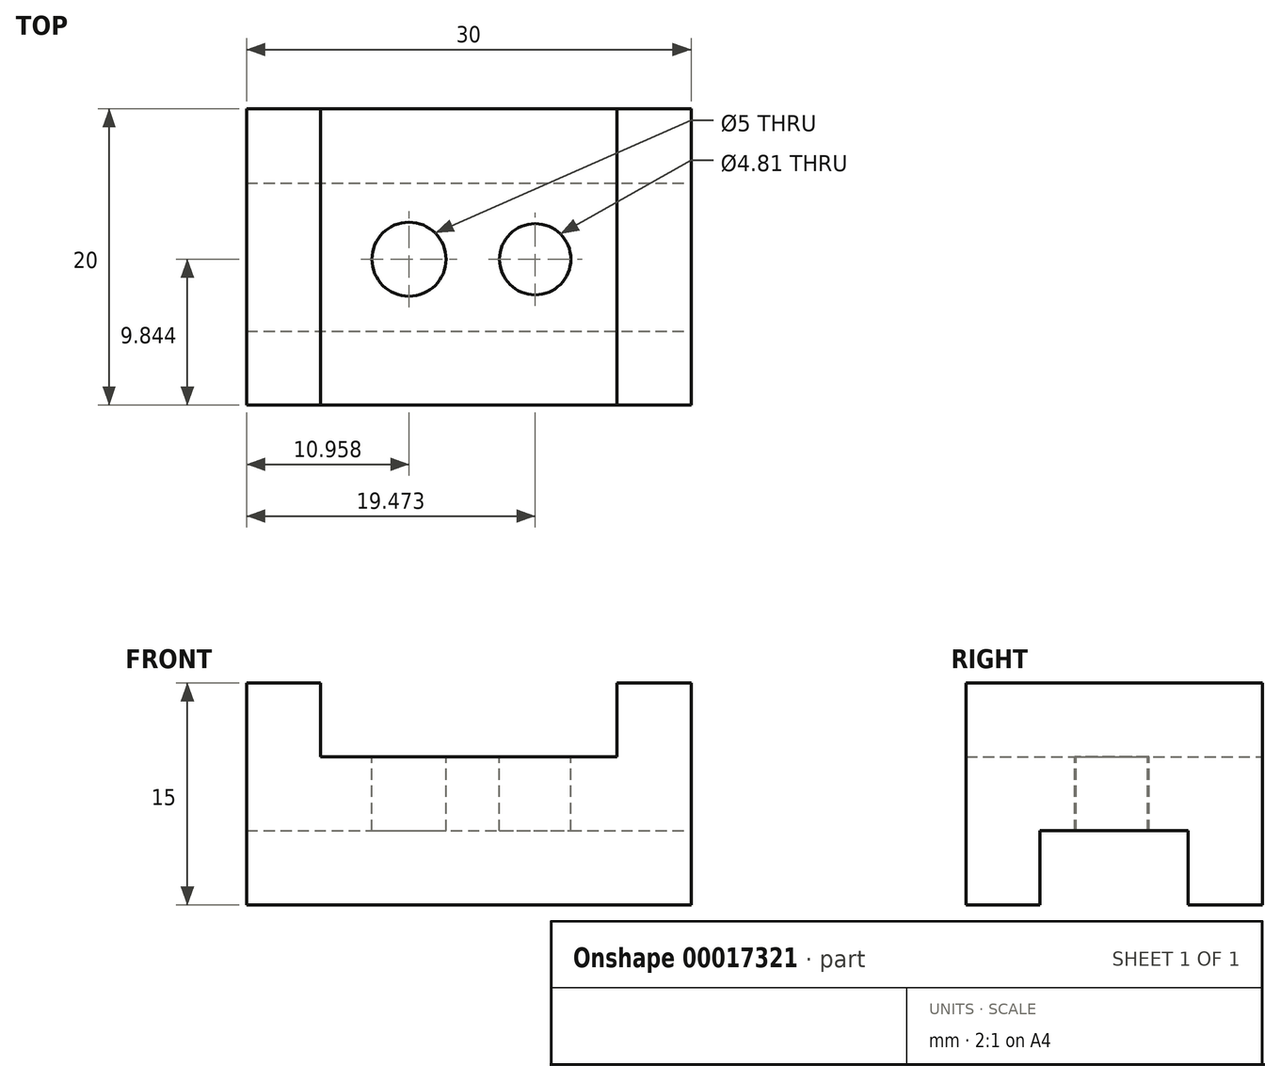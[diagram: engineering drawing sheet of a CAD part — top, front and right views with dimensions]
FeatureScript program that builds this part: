
annotation { "Feature Type Name" : "Feature", "Feature Type Description" : "" }
export const myFeature = defineFeature(function(context is Context, id is Id, definition is map)
    precondition{}
    {
        {
            var Q0;
            Q0=qCreatedBy(makeId("Front.planeOp"),FACE);
            var sketch = newSketch(context, id + "F0", { "sketchPlane" : qUnion([Q0])});
            skLineSegment(sketch, "E0", {"start": v(-34.67, 12.97) * mm, "end": v(-34.67, -2.03) * mm});
            skLineSegment(sketch, "E1", {"start": v(-34.67, 12.97) * mm, "end": v(-29.67, 12.97) * mm});
            skLineSegment(sketch, "E2", {"start": v(-29.67, 12.97) * mm, "end": v(-29.67, 7.97) * mm});
            skLineSegment(sketch, "E3", {"start": v(-29.67, 7.97) * mm, "end": v(-9.67, 7.97) * mm});
            skLineSegment(sketch, "E4", {"start": v(-9.67, 7.97) * mm, "end": v(-9.67, 12.97) * mm});
            skLineSegment(sketch, "E5", {"start": v(-4.67, 12.97) * mm, "end": v(-4.67, -2.03) * mm});
            skLineSegment(sketch, "E6", {"start": v(-4.67, -2.03) * mm, "end": v(-34.67, -2.03) * mm});
            skLineSegment(sketch, "E7", {"start": v(-4.67, 12.97) * mm, "end": v(-9.67, 12.97) * mm});
            skSolve(sketch);
        }
        {
            var Q0;
            Q0=makeQuery(id+"F0.imprint","IMPRINT",FACE,{"disambiguationData":[TD([[makeQuery(id+"F0.imprint","IMPRINT",EDGE,{"derivedFrom":sQuery(id+"F0.wireOp",EDGE,"E0")}),1.0]])]});
            extrude(context, id + "F1", {"entities" : qUnion([Q0]), "depth" : 20 * mm});
        }
        {
            var Q0;
            Q0=makeQuery(id+"F1.opExtrude","SWEPT_FACE",FACE,{"disambiguationData":[OSD([sQuery(id+"F0.wireOp",EDGE,"E3")])]});
            var sketch = newSketch(context, id + "F2", { "sketchPlane" : qUnion([Q0])});
            skCircle(sketch, "E8", {"center": v(-23.71, -10.16) * mm, "radius": 2.5 * mm});
            skCircle(sketch, "E9", {"center": v(-15.2, -10.16) * mm, "radius": 2.4 * mm});
            skSolve(sketch);
        }
        {
            var Q0;
            Q0=makeQuery(id+"F2.imprint","IMPRINT",FACE,{"disambiguationData":[TD([[makeQuery(id+"F2.imprint","IMPRINT",EDGE,{"derivedFrom":sQuery(id+"F2.wireOp",EDGE,"E9")}),1.0]])]});
            var Q1;
            Q1=makeQuery(id+"F2.imprint","IMPRINT",FACE,{"disambiguationData":[TD([[makeQuery(id+"F2.imprint","IMPRINT",EDGE,{"derivedFrom":sQuery(id+"F2.wireOp",EDGE,"E8")}),1.0]])]});
            extrude(context, id + "F3", {"entities" : qUnion([Q0, Q1]), "operationType" : NewBodyOperationType.REMOVE, "endBound" : BoundingType.THROUGH_ALL, "oppositeDirection" : true, "depth" : 25 * mm});
        }
        {
            var Q0;
            Q0=makeQuery(id+"F1.opExtrude","SWEPT_FACE",FACE,{"disambiguationData":[OSD([sQuery(id+"F0.wireOp",EDGE,"E5")])]});
            var sketch = newSketch(context, id + "F4", { "sketchPlane" : qUnion([Q0])});
            skLineSegment(sketch, "E10", {"start": v(-20, -2.03) * mm, "end": v(-15, -2.03) * mm});
            skLineSegment(sketch, "E11", {"start": v(-15, -2.03) * mm, "end": v(-5, -2.03) * mm});
            skLineSegment(sketch, "E12", {"start": v(-15, -2.03) * mm, "end": v(-15, 2.97) * mm});
            skLineSegment(sketch, "E13", {"start": v(-15, 2.97) * mm, "end": v(-5, 2.97) * mm});
            skLineSegment(sketch, "E14", {"start": v(-5, 2.97) * mm, "end": v(-5, -2.03) * mm});
            skSolve(sketch);
        }
        {
            var Q0;
            Q0=makeQuery(id+"F4.imprint","IMPRINT",FACE,{"disambiguationData":[TD([[makeQuery(id+"F4.imprint","IMPRINT",EDGE,{"derivedFrom":sQuery(id+"F4.wireOp",EDGE,"E11")}),1.0]])]});
            extrude(context, id + "F5", {"entities" : qUnion([Q0]), "operationType" : NewBodyOperationType.REMOVE, "endBound" : BoundingType.THROUGH_ALL, "oppositeDirection" : true, "depth" : 25 * mm});
        }
    });
